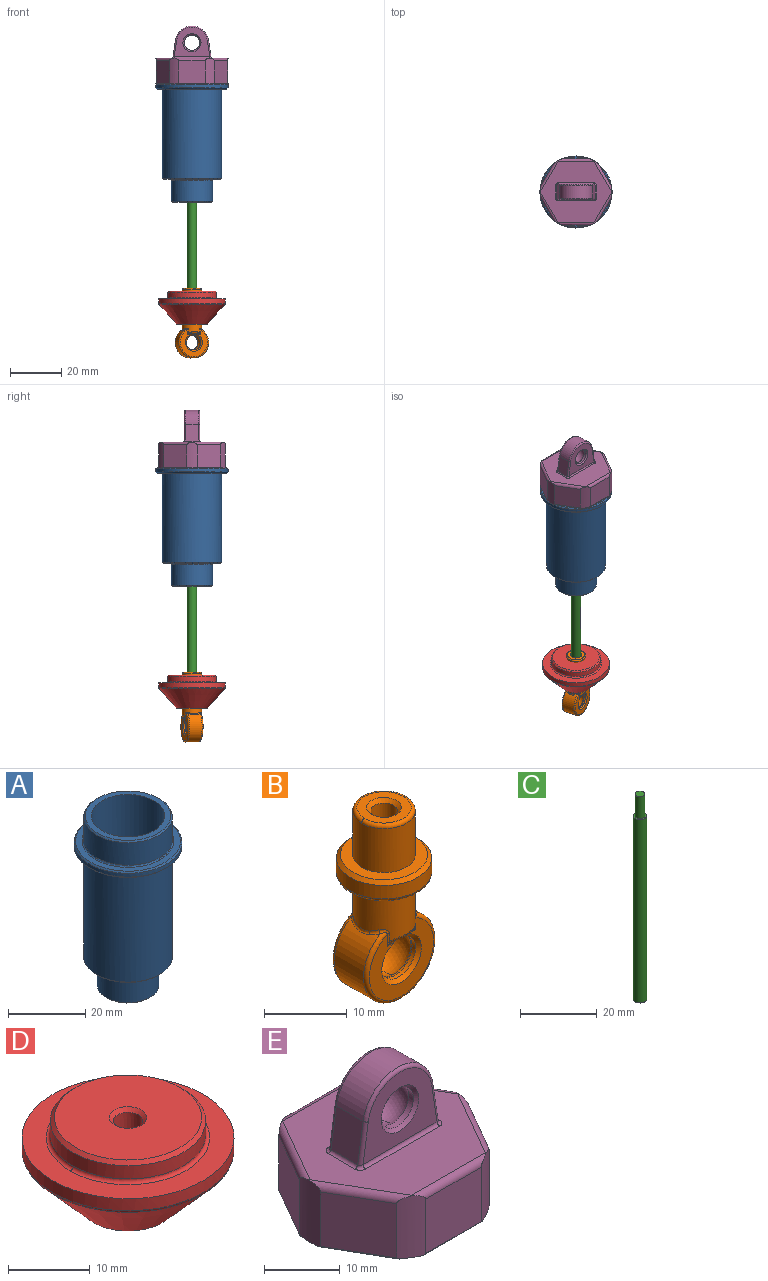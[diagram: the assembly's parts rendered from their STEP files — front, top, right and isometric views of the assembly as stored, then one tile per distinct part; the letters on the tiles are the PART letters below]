
ASSEMBLY  parts=5 mates=4
PART A: 28 faces, bbox 28x28x54.1 mm
  f0: torus R=9.1mm, axis (0,0,-1), area 18.5mm2, adj f4,f18,f19
  f1: torus R=11.9mm, axis (0,0,-1), area 23mm2, adj f6,f20,f22
  f2: torus R=5.6mm, axis (0,0,-1), area 11.6mm2, adj f9,f21,f23
  f3: torus R=8.4mm, axis (0,0,-1), area 16.1mm2, adj f15,f26,f27
  f4: cylinder r=9.5mm len=42.6mm, axis (0,0,-1), area 2542.8mm2, adj f0,f17,f18
  f5: cone r=11.5mm half-angle=45deg, axis (0,0,-1), area 40.2mm2, adj f6,f17
  f6: cylinder r=11.5mm len=23mm, axis (0,0,-1), area 520.2mm2, adj f1,f5,f20
  f7: cylinder r=3.78mm len=7.56mm, axis (0,0,-1), area 49.9mm2, adj f19,f21
  f8: cone r=14mm half-angle=45deg, axis (0,0,-1), area 49mm2, adj f10,f22
  f9: cylinder r=6mm len=12mm, axis (0,0,-1), area 309.1mm2, adj f2,f11,f23
  f10: cylinder r=14mm len=28mm, axis (0,0,-1), area 105.6mm2, adj f8,f12
  f11: cone r=6.4mm half-angle=45deg, axis (0,0,-1), area 22mm2, adj f9,f24
  f12: cone r=14mm half-angle=45deg, axis (0,0,1), area 49mm2, adj f10,f25
  f13: cone r=8mm half-angle=45deg, axis (0,0,1), area 27.7mm2, adj f15,f24
  f14: cylinder r=11.5mm len=34.7mm, axis (0,0,-1), area 2507.3mm2, adj f16,f25
  f15: cylinder r=8mm len=16mm, axis (0,0,-1), area 412.2mm2, adj f3,f13,f26
  f16: cone r=11.5mm half-angle=45deg, axis (0,0,1), area 40.2mm2, adj f14,f27
  f17: plane 22.2x22.2mm, normal (0,0,1), area 103.5mm2, adj f4,f5
  f18: torus R=9.1mm, axis (0,0,-1), area 18.5mm2, adj f0,f4,f19
  f19: plane 18.2x18.2mm, normal (0,0,1), area 215.3mm2, adj f0,f7,f18
  f20: torus R=11.9mm, axis (0,0,-1), area 23mm2, adj f1,f6,f22
  f21: plane 11.2x11.2mm, normal (0,0,-1), area 53.6mm2, adj f2,f7,f23
  f22: plane 27.2x27.2mm, normal (0,0,1), area 136.2mm2, adj f1,f8,f20
  f23: torus R=5.6mm, axis (0,0,-1), area 11.6mm2, adj f2,f9,f21
  f24: plane 15.2x15.2mm, normal (0,0,-1), area 52.8mm2, adj f11,f13
  f25: plane 27.2x27.2mm, normal (0,0,-1), area 165.6mm2, adj f12,f14
  f26: torus R=8.4mm, axis (0,0,-1), area 16.1mm2, adj f3,f15,f27
  f27: plane 22.2x22.2mm, normal (0,0,-1), area 165.4mm2, adj f3,f16,f26
PART B: 54 faces, bbox 13x12.5x27.5 mm
  f0: torus R=4.29mm, axis (0,0,1), area 9.8mm2, adj f5,f28,f42
  f1: torus R=5.29mm, axis (0,0,1), area 13.8mm2, adj f11,f42,f46
  f2: sphere r=3.4mm, area 35.6mm2, adj f10,f47,f49
  f3: torus R=3.29mm, axis (0,0,1), area 8.9mm2, adj f13,f51,f52
  f4: cylinder r=6mm len=12mm, axis (0,-1,0), area 148.5mm2, adj f16,f17,f18,f19,f20,f21
  f5: cylinder r=3.79mm len=7.57mm, axis (0,0,1), area 140.6mm2, adj f0,f17,f18,f20,f21,f24,f25,f26
  f6: cone r=3.4mm half-angle=45deg, axis (0,-1,0), area 12.4mm2, adj f8,f22,f32,f33
  f7: cone r=3.4mm half-angle=45deg, axis (0,1,0), area 12.4mm2, adj f9,f23,f43,f44
  f8: cylinder r=2.9mm len=5.8mm, axis (0,-1,0), area 10.8mm2, adj f6,f10,f32,f33
  f9: cylinder r=2.9mm len=5.8mm, axis (0,-1,0), area 10.8mm2, adj f7,f43,f44,f47,f48
  f10: cone r=2.96mm half-angle=14.7deg, axis (0,1,0), area 4.7mm2, adj f2,f8,f49
  f11: cylinder r=5.79mm len=11.57mm, axis (0,0,1), area 72.7mm2, adj f1,f12,f46
  f12: cone r=5.79mm half-angle=45deg, axis (0,0,-1), area 24.6mm2, adj f11,f50
  f13: cylinder r=3.79mm len=7.57mm, axis (0,0,1), area 154.6mm2, adj f3,f50,f51
  f14: cone r=2.1mm half-angle=45deg, axis (0,0,1), area 8.2mm2, adj f15,f52
  f15: cylinder r=1.6mm len=14.5mm, axis (0,0,1), area 145.8mm2, adj f14,f53
  f16: torus R=5.5mm, axis (0,-1,0), area 24.2mm2, adj f4,f22,f40,f41
  f17: bspline ~1.43x0.89mm, area 0.7mm2, adj f4,f5,f18,f41
  f18: bspline ~3.74x1.06mm, area 1.9mm2, adj f4,f5,f17,f27
  f19: torus R=5.5mm, axis (0,-1,0), area 24.2mm2, adj f4,f23,f27,f29
  f20: bspline ~3.78x1.11mm, area 1.9mm2, adj f4,f5,f21,f29
  f21: bspline ~1.41x0.89mm, area 0.7mm2, adj f4,f5,f20,f40
  f22: plane 11x10.42mm, normal (0,-1,0), area 48.5mm2, adj f6,f16,f24,f25,f45
  f23: plane 11x10.42mm, normal (0,1,0), area 48.5mm2, adj f7,f19,f30,f31,f37
  f24: cylinder r=0.5mm len=1.74mm, axis (0,0,-1), area 0.4mm2, adj f5,f22,f34,f41
  f25: cylinder r=0.5mm len=1.74mm, axis (0,0,1), area 0.4mm2, adj f5,f22,f35,f40
  f26: bspline ~4.55x0.85mm, area 2.5mm2, adj f5,f36,f37,f38
  f27: bspline ~1.2x1.09mm, area 0.6mm2, adj f5,f18,f19,f30
  f28: torus R=4.29mm, axis (0,0,1), area 9.8mm2, adj f0,f5,f42
  f29: bspline ~1.19x1.08mm, area 0.6mm2, adj f5,f19,f20,f31
  f30: cylinder r=0.5mm len=1.74mm, axis (0,0,1), area 0.4mm2, adj f5,f23,f27,f38
  f31: cylinder r=0.5mm len=1.74mm, axis (0,0,-1), area 0.4mm2, adj f5,f23,f29,f36
  f32: bspline ~1.4x0.63mm, area 0.8mm2, adj f6,f8,f33,f45
  f33: bspline ~1.4x0.63mm, area 0.8mm2, adj f6,f8,f32,f45
  f34: bspline ~0.84x0.58mm, area 0.1mm2, adj f24,f39,f45
  f35: bspline ~0.84x0.58mm, area 0.1mm2, adj f25,f39,f45
  f36: bspline ~0.84x0.58mm, area 0.1mm2, adj f26,f31,f37
  f37: cylinder r=0.5mm len=4.94mm, axis (1,0,0), area 2.2mm2, adj f23,f26,f36,f38,f43,f44
  f38: bspline ~0.84x0.58mm, area 0.1mm2, adj f26,f30,f37
  f39: bspline ~4.55x0.87mm, area 2.5mm2, adj f5,f34,f35,f45
  f40: bspline ~1.2x1.09mm, area 0.6mm2, adj f5,f16,f21,f25
  f41: bspline ~1.2x1.09mm, area 0.6mm2, adj f5,f16,f17,f24
  f42: plane 10.57x10.57mm, normal (0,0,-1), area 30.1mm2, adj f0,f1,f28,f46
  f43: bspline ~1.4x0.63mm, area 0.8mm2, adj f7,f9,f37,f44
  f44: bspline ~1.43x0.63mm, area 0.8mm2, adj f7,f9,f37,f43
  f45: cylinder r=0.5mm len=4.94mm, axis (-1,0,0), area 2.2mm2, adj f22,f32,f33,f34,f35,f39
  f46: torus R=5.29mm, axis (0,0,1), area 13.8mm2, adj f1,f11,f42
  f47: cone r=2.96mm half-angle=14.7deg, axis (0,-1,0), area 2.3mm2, adj f2,f9,f48
  f48: cone r=2.96mm half-angle=14.7deg, axis (0,-1,0), area 2.3mm2, adj f9,f47,f49
  f49: sphere r=3.4mm, area 35.6mm2, adj f2,f10,f48
  f50: plane 10.57x10.57mm, normal (0,0,1), area 42.7mm2, adj f12,f13
  f51: torus R=3.29mm, axis (0,0,1), area 8.9mm2, adj f3,f13,f52
  f52: plane 6.57x6.57mm, normal (0,0,1), area 20.1mm2, adj f3,f14,f51
  f53: plane 3.2x3.2mm, normal (0,0,1), area 8mm2, adj f15
PART C: 5 faces, bbox 3.6x3.6x65.5 mm
  f0: cylinder r=1.78mm len=58.5mm, axis (0,0,-1), area 654.3mm2, adj f2,f3
  f1: cylinder r=1.3mm len=7mm, axis (0,0,-1), area 57.2mm2, adj f3,f4
  f2: plane 3.56x3.56mm, normal (0,0,-1), area 10mm2, adj f0
  f3: plane 3.56x3.56mm, normal (0,0,1), area 4.6mm2, adj f0,f1
  f4: plane 2.6x2.6mm, normal (0,0,1), area 5.3mm2, adj f1
PART D: 18 faces, bbox 28.1x28.1x13 mm
  f0: torus R=5.55mm, axis (0,0,1), area 7.5mm2, adj f3,f11,f13
  f1: torus R=12.5mm, axis (0,0,1), area 15mm2, adj f3,f4,f12
  f2: torus R=10.02mm, axis (0,0,1), area 23.9mm2, adj f7,f14,f15
  f3: cone r=12.87mm half-angle=42.1deg, axis (0,0,1), area 612.1mm2, adj f0,f1,f11,f12
  f4: cylinder r=13mm len=26mm, axis (0,0,1), area 147.5mm2, adj f1,f12,f14
  f5: cone r=4.27mm half-angle=45deg, axis (0,0,-1), area 17.9mm2, adj f6,f13
  f6: cylinder r=3.77mm len=7.54mm, axis (0,0,1), area 154mm2, adj f5,f16
  f7: cylinder r=9.53mm len=19.05mm, axis (0,0,1), area 119.7mm2, adj f2,f9,f15
  f8: cone r=1.8mm half-angle=0deg, axis (0,0,1), area 62.3mm2, adj f10,f16
  f9: cone r=9.53mm half-angle=45deg, axis (0,0,-1), area 41.2mm2, adj f7,f17
  f10: cone r=2.31mm half-angle=45deg, axis (0,0,1), area 9.1mm2, adj f8,f17
  f11: torus R=5.55mm, axis (0,0,1), area 7.5mm2, adj f0,f3,f13
  f12: torus R=12.5mm, axis (0,0,1), area 15mm2, adj f1,f3,f4
  f13: plane 11.1x11.1mm, normal (0,0,-1), area 39.4mm2, adj f0,f5,f11
  f14: plane 26x26mm, normal (0,0,1), area 215.2mm2, adj f2,f4,f15
  f15: torus R=10.02mm, axis (0,0,1), area 23.9mm2, adj f2,f7,f14
  f16: plane 7.54x7.54mm, normal (0,0,-1), area 34.5mm2, adj f6,f8
  f17: plane 18.05x18.05mm, normal (0,0,1), area 239.2mm2, adj f9,f10
PART E: 56 faces, bbox 29.6x26.1x23.1 mm
  f0: sphere r=3.4mm, area 33.8mm2, adj f4,f5,f53
  f1: torus R=10.05mm, axis (0,0,-1), area 10mm2, adj f7,f54,f55
  f2: cone r=3.51mm half-angle=45deg, axis (0,-1,0), area 14.5mm2, adj f4,f23
  f3: cone r=3.51mm half-angle=45deg, axis (0,1,0), area 14.5mm2, adj f5,f25
  f4: cylinder r=3.01mm len=6.02mm, axis (0,1,0), area 17.4mm2, adj f0,f2,f53
  f5: cylinder r=3.01mm len=6.02mm, axis (0,1,0), area 17.4mm2, adj f0,f3,f53
  f6: cone r=10.75mm half-angle=45deg, axis (0,0,-1), area 46.7mm2, adj f7,f46
  f7: cylinder r=10.25mm len=20.5mm, axis (0,0,-1), area 470.1mm2, adj f1,f6,f54
  f8: plane 27.77x24.06mm, normal (0,0,1), area 388.7mm2, adj f9,f10,f11,f12,f13,f14,f15,f16
  f9: bspline ~1.09x1.01mm, area 0.8mm2, adj f8,f10,f16,f41
  f10: cylinder r=0.5mm len=13.85mm, axis (1,0,0), area 10.9mm2, adj f8,f9,f11,f23
  f11: bspline ~1.09x1.02mm, area 0.8mm2, adj f8,f10,f12,f39
  f12: cylinder r=0.5mm len=5mm, axis (0,-1,0), area 3.5mm2, adj f8,f11,f13,f24
  f13: bspline ~1.09x1.01mm, area 0.8mm2, adj f8,f12,f14,f42
  f14: cylinder r=0.5mm len=13.85mm, axis (-1,0,0), area 10.9mm2, adj f8,f13,f15,f25
  f15: bspline ~1.09x1.02mm, area 0.8mm2, adj f8,f14,f16,f45
  f16: cylinder r=0.5mm len=5mm, axis (0,-1,0), area 3.5mm2, adj f8,f9,f15,f26
  f17: cylinder r=1mm len=14mm, axis (-1,0,0), area 18.8mm2, adj f8,f18,f22,f27,f28,f29
  f18: cylinder r=1mm len=12.62mm, axis (-0.5,-0.87,0), area 18.8mm2, adj f8,f17,f19,f28,f30,f31
  f19: cylinder r=1mm len=12.62mm, axis (0.5,-0.87,0), area 18.8mm2, adj f8,f18,f20,f30,f32,f33
  f20: cylinder r=1mm len=14mm, axis (1,0,0), area 18.8mm2, adj f8,f19,f21,f32,f34,f35
  f21: cylinder r=1mm len=12.62mm, axis (0.5,0.87,0), area 18.8mm2, adj f8,f20,f22,f34,f36,f37
  f22: cylinder r=1mm len=12.62mm, axis (-0.5,0.87,0), area 18.8mm2, adj f8,f17,f21,f27,f36,f38
  f23: plane 13.84x11.5mm, normal (0,-1,0), area 89.3mm2, adj f2,f10,f39,f40,f41
  f24: plane 6.57x5mm, normal (-0.99,0,0.15), area 33.2mm2, adj f12,f39,f42,f43
  f25: plane 13.83x11.5mm, normal (0,1,0), area 89.3mm2, adj f3,f14,f42,f44,f45
  f26: plane 6.57x5mm, normal (0.99,0,0.15), area 33.2mm2, adj f16,f41,f43,f45
  f27: cylinder r=14mm len=9.99mm, axis (0,0,-1), area 39mm2, adj f17,f22,f29,f38,f46,f47,f52
  f28: cylinder r=14mm len=9.99mm, axis (0,0,-1), area 39mm2, adj f17,f18,f29,f31,f46,f47,f48
  f29: plane 10.39x8.8mm, normal (0,1,0), area 91.5mm2, adj f17,f27,f28,f47
  f30: cylinder r=14mm len=9.99mm, axis (0,0,-1), area 39mm2, adj f18,f19,f31,f33,f46,f48,f49
  f31: plane 9x8.8mm, normal (-0.87,0.5,0), area 91.5mm2, adj f18,f28,f30,f48
  f32: cylinder r=14mm len=9.99mm, axis (0,0,-1), area 39mm2, adj f19,f20,f33,f35,f46,f49,f50
  f33: plane 9x8.8mm, normal (-0.87,-0.5,0), area 91.5mm2, adj f19,f30,f32,f49
  f34: cylinder r=14mm len=9.99mm, axis (0,0,-1), area 39mm2, adj f20,f21,f35,f37,f46,f50,f51
  f35: plane 10.39x8.8mm, normal (0,-1,0), area 91.5mm2, adj f20,f32,f34,f50
  f36: cylinder r=14mm len=9.99mm, axis (0,0,-1), area 39mm2, adj f21,f22,f37,f38,f46,f51,f52
  f37: plane 9x8.8mm, normal (0.87,-0.5,0), area 91.5mm2, adj f21,f34,f36,f51
  f38: plane 9x8.8mm, normal (0.87,0.5,0), area 91.5mm2, adj f22,f27,f36,f52
  f39: cylinder r=0.5mm len=6.64mm, axis (-0.15,0,-0.99), area 5.2mm2, adj f11,f23,f24,f40
  f40: torus R=6mm, axis (0,-1,0), area 14.1mm2, adj f23,f39,f41,f43
  f41: cylinder r=0.5mm len=6.64mm, axis (-0.15,0,0.99), area 5.2mm2, adj f9,f23,f26,f40
  f42: cylinder r=0.5mm len=6.64mm, axis (0.15,0,0.99), area 5.2mm2, adj f13,f24,f25,f44
  f43: cylinder r=6.5mm len=12.85mm, axis (0,-1,0), area 92.2mm2, adj f24,f26,f40,f44
  f44: torus R=6mm, axis (0,-1,0), area 14.1mm2, adj f25,f42,f43,f45
  f45: cylinder r=0.5mm len=6.64mm, axis (0.15,0,-0.99), area 5.2mm2, adj f15,f25,f26,f44
  f46: plane 28x25.6mm, normal (0,0,-1), area 197.8mm2, adj f6,f27,f28,f30,f32,f34,f36,f47
  f47: cylinder r=0.2mm len=11.34mm, axis (1,0,0), area 3.4mm2, adj f27,f28,f29,f46
  f48: cylinder r=0.2mm len=9.92mm, axis (0.5,0.87,0), area 3.4mm2, adj f28,f30,f31,f46
  f49: cylinder r=0.2mm len=9.92mm, axis (-0.5,0.87,0), area 3.4mm2, adj f30,f32,f33,f46
  f50: cylinder r=0.2mm len=11.34mm, axis (-1,0,0), area 3.4mm2, adj f32,f34,f35,f46
  f51: cylinder r=0.2mm len=9.92mm, axis (-0.5,-0.87,0), area 3.4mm2, adj f34,f36,f37,f46
  f52: cylinder r=0.2mm len=9.92mm, axis (0.5,-0.87,0), area 3.4mm2, adj f27,f36,f38,f46
  f53: sphere r=3.4mm, area 33.8mm2, adj f0,f4,f5
  f54: torus R=10.05mm, axis (0,0,-1), area 10mm2, adj f1,f7,f55
  f55: plane 20.1x20.1mm, normal (0,0,-1), area 317.3mm2, adj f1,f54
PLACE A at identity
PLACE B rot(axis=(0,0,1),14.7deg) t=(0,0,-116.53)mm
PLACE C rot(axis=(0,0,1),90deg) t=(0,0,8.5)mm
PLACE D rot(axis=(0,0,-1),117.4deg) t=(0,0,-130.77)mm
PLACE E at identity
MATE revolute C.f0 <-> D.f11  axis (0,0,-1) through (0,0,-101.5)mm
MATE revolute E.f6 <-> A.f18  axis (0,0,-1) through (0,0,-16)mm
MATE cylindrical C.f0 <-> A.f20  axis (0,0,1) through (0,0,-43)mm
MATE revolute B.f0 <-> D.f11  axis (0,0,1) through (0,0,-102.5)mm
